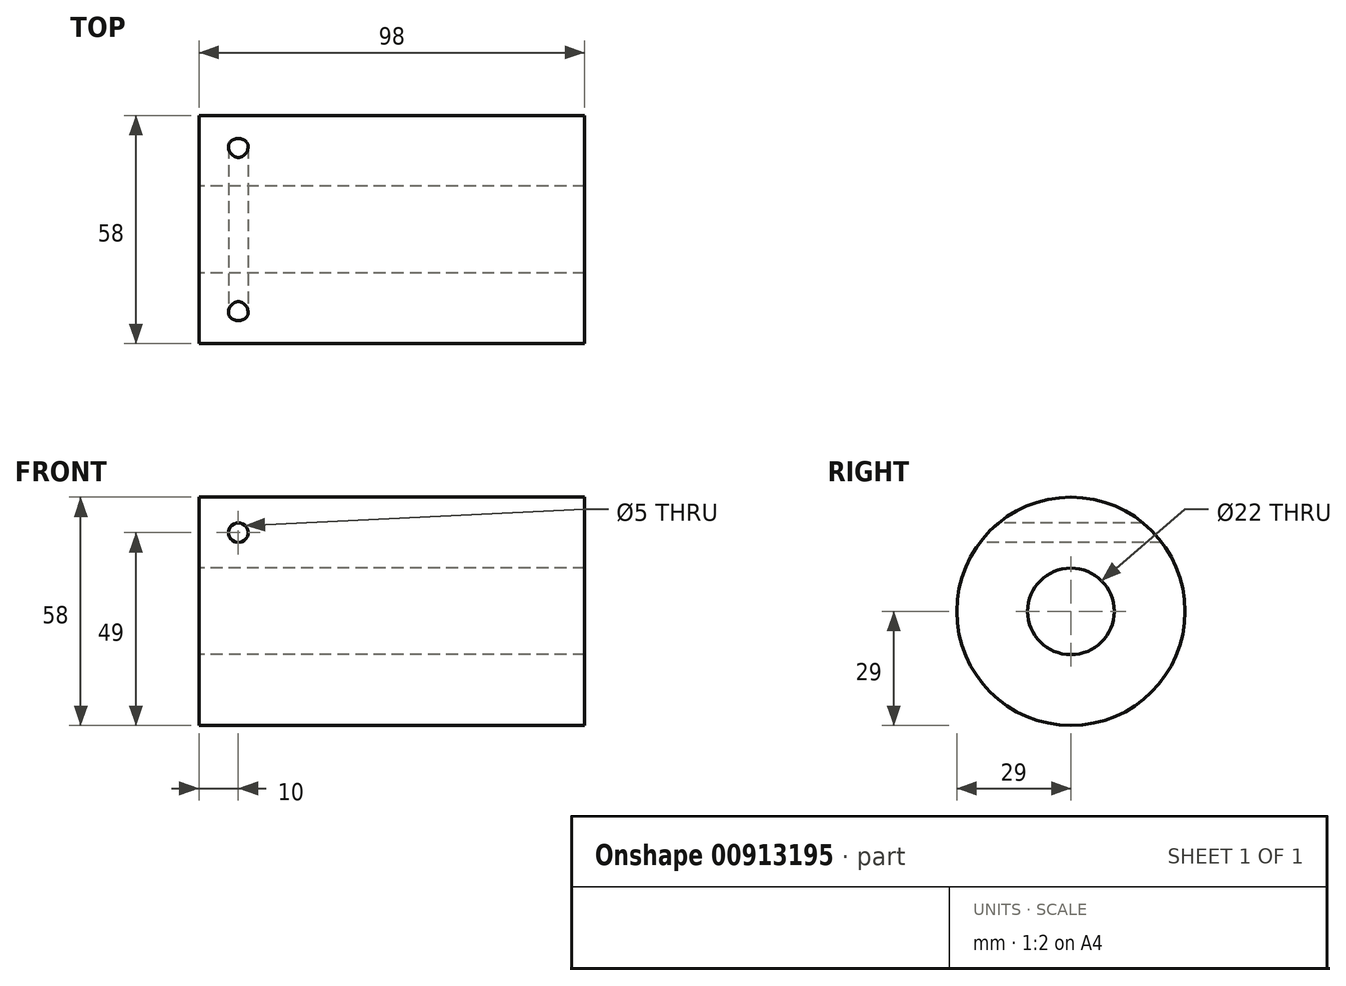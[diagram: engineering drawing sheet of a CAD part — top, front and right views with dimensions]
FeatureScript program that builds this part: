
annotation { "Feature Type Name" : "Feature", "Feature Type Description" : "" }
export const myFeature = defineFeature(function(context is Context, id is Id, definition is map)
    precondition{}
    {
        {
            var Q0;
            Q0=qCreatedBy(makeId("Front.planeOp"),FACE);
            var sketch = newSketch(context, id + "F0", { "sketchPlane" : qUnion([Q0])});
            skLineSegment(sketch, "E0.bottom", {"start": v(-49, 29) * mm, "end": v(49, 29) * mm});
            skLineSegment(sketch, "E0.top", {"start": v(-49, 11) * mm, "end": v(49, 11) * mm});
            skLineSegment(sketch, "E0.left", {"start": v(-49, 29) * mm, "end": v(-49, 11) * mm});
            skLineSegment(sketch, "E0.right", {"start": v(49, 29) * mm, "end": v(49, 11) * mm});
            skLineSegment(sketch, "E1", {"start": v(-45.93, 0) * mm, "end": v(103.2, 0) * mm, "construction": true});
            skSolve(sketch);
        }
        {
            var Q0;
            Q0=makeQuery(id+"F0.imprint","IMPRINT",FACE,{"disambiguationData":[TD([[makeQuery(id+"F0.imprint","IMPRINT",EDGE,{"derivedFrom":sQuery(id+"F0.wireOp",EDGE,"E0.bottom")}),-1.0]])]});
            var Q1;
            Q1=sQuery(id+"F0.wireOp",EDGE,"E1");
            revolve(context, id + "F1", {"surfaceOperationType" : NewSurfaceOperationType.NEW, "entities" : qUnion([Q0]), "axis" : qUnion([Q1]), "revolveType" : RevolveType.FULL});
        }
        {
            var Q0;
            Q0=qCreatedBy(makeId("Front.planeOp"),FACE);
            cPlane(context, id + "F2", {"entities" : qUnion([Q0]), "cplaneType" : CPlaneType.OFFSET, "offset" : 25 * mm, "width" : 150 * mm, "height" : 150 * mm});
        }
        {
            var Q0;
            Q0=qCreatedBy(id+"F2.planeOp",FACE);
            var sketch = newSketch(context, id + "F3", { "sketchPlane" : qUnion([Q0])});
            skCircle(sketch, "E2", {"center": v(-39, 20) * mm, "radius": 3.25 * mm});
            skSolve(sketch);
        }
        {
            var Q0;
            Q0=sQuery(id+"F3.wireOp",VERTEX,"E2.center");
            var Q1;
            Q1=makeQuery(id+"F1.opRevolve","SWEPT_BODY",BODY,{"disambiguationData":[OSD([sQuery(id+"F0.wireOp",EDGE,"E0.bottom"),sQuery(id+"F0.wireOp",EDGE,"E0.top"),sQuery(id+"F0.wireOp",EDGE,"E0.left"),sQuery(id+"F0.wireOp",EDGE,"E0.right")])]});
            hole(context, id + "F4", {"style" : HoleStyle.SIMPLE, "endStyle" : HoleEndStyle.THROUGH, "holeDiameter" : 5 * mm, "majorDiameter" : 5 * mm, "isTappedThrough" : true, "tappedDepth" : 12 * mm, "tapClearance" : 3, "locations" : qUnion([Q0]), "scope" : qUnion([Q1])});
        }
    });
